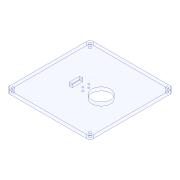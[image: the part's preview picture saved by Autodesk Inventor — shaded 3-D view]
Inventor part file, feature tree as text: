
AUTODESK INVENTOR PART (.ipt)
format: ipt  version: 2020 (Build 240168000, 168)  size: 136,704 bytes
history: native  units: mm
features: extrude x3, sketch x3, fillet x1
ambient origin geometry x8: Origin, YZ Plane, XZ Plane, XY Plane, X Axis, Y Axis, Z Axis, Center Point
bodies: Solid1 (feature_tree)
feature tree (7):
  extrude  "Extrusion1"  Depth=120.0mm
  extrude  "Extrusion2"  Depth=5.0mm
  fillet  "Fillet1"  Radius=110.0mm
  extrude  "Extrusion3"  Depth=4.0mm
  sketch  "Sketch1"  dims[d0=120.0mm d1=120.0mm]
  sketch  "Sketch2"  dims[d2=5.0mm d3=0.0mm d4=110.0mm d5=110.0mm]
  sketch  "Sketch4"  dims[d6=4.0mm d7=4.0mm d8=4.0mm d9=4.0mm d10=5.0mm d11=0.0mm d12=5.0mm d14=4.0mm d15=15.0mm d16=20.0mm d17=14.0mm d18=14.0mm d19=2.5mm d20=2.5mm d21=8.5mm d22=4.25mm d23=10.0mm d24=0.0mm d25=26.5mm]
